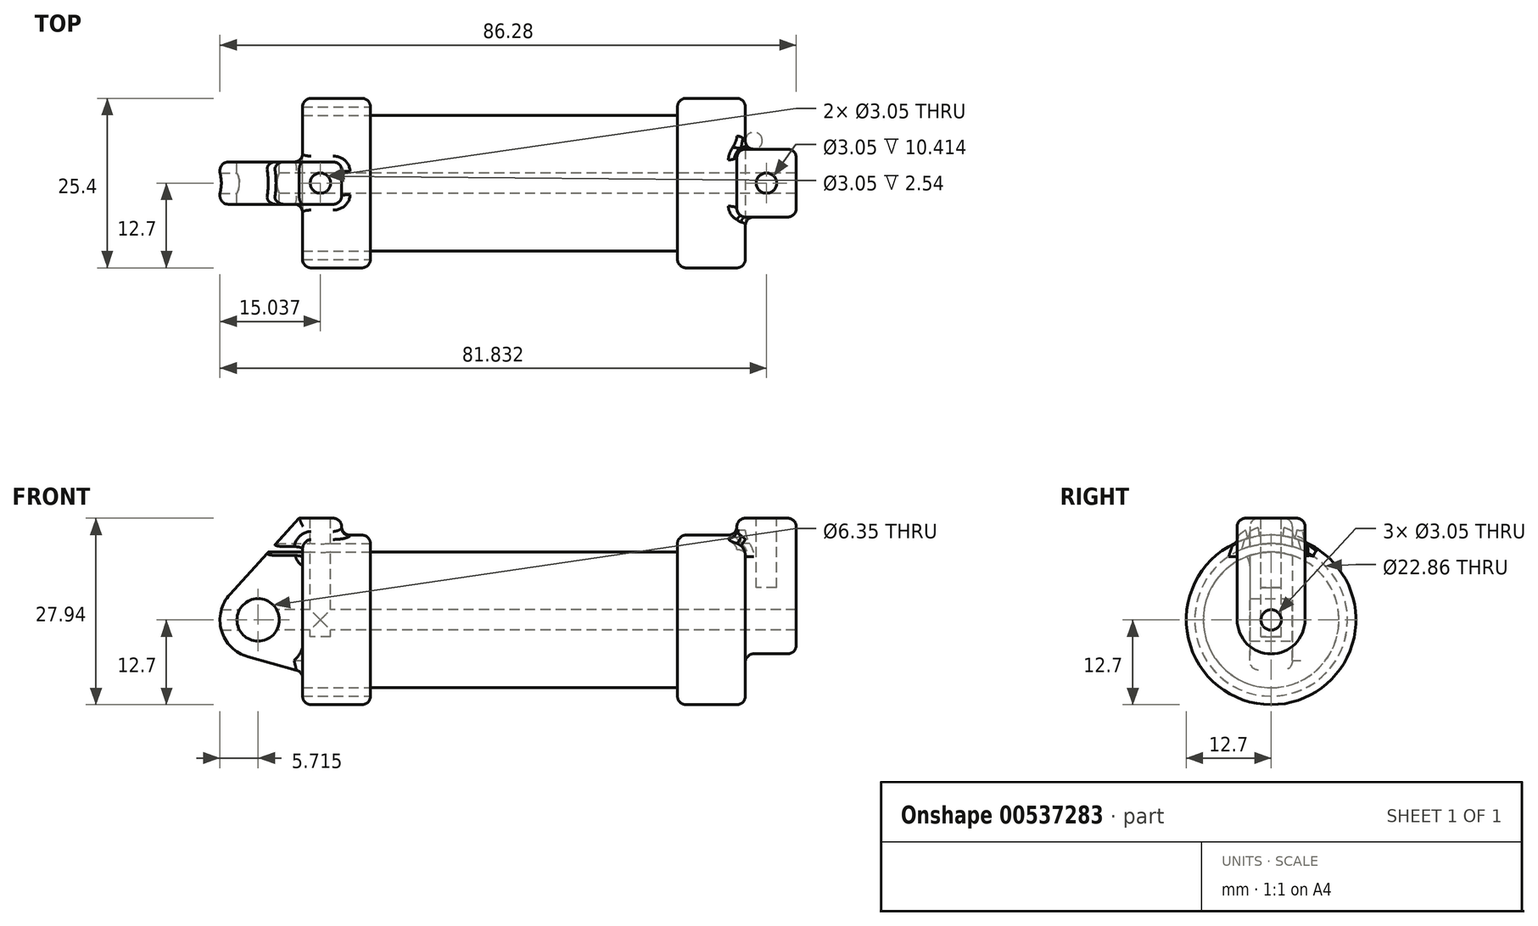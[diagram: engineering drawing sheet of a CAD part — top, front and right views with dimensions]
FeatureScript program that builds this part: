
annotation { "Feature Type Name" : "Feature", "Feature Type Description" : "" }
export const myFeature = defineFeature(function(context is Context, id is Id, definition is map)
    precondition{}
    {
        {
            var Q0;
            Q0=qCreatedBy(makeId("Front.planeOp"),FACE);
            var sketch = newSketch(context, id + "F0", { "sketchPlane" : qUnion([Q0])});
            skLineSegment(sketch, "E0", {"start": v(0, 0) * mm, "end": v(0, 12.7) * mm});
            skLineSegment(sketch, "E1", {"start": v(0, 12.7) * mm, "end": v(10.16, 12.7) * mm});
            skLineSegment(sketch, "E2", {"start": v(10.16, 12.7) * mm, "end": v(10.16, 10.16) * mm});
            skLineSegment(sketch, "E3", {"start": v(10.16, 10.16) * mm, "end": v(56.13, 10.16) * mm});
            skLineSegment(sketch, "E4", {"start": v(56.13, 10.16) * mm, "end": v(56.13, 12.7) * mm});
            skLineSegment(sketch, "E5", {"start": v(56.13, 12.7) * mm, "end": v(66.3, 12.7) * mm});
            skLineSegment(sketch, "E6", {"start": v(66.3, 12.7) * mm, "end": v(66.3, 0) * mm});
            skLineSegment(sketch, "E7", {"start": v(66.3, 0) * mm, "end": v(0, 0) * mm});
            skLineSegment(sketch, "E8", {"start": v(5.84, 15.24) * mm, "end": v(-0.5, 15.24) * mm});
            skLineSegment(sketch, "E9", {"start": v(-0.5, 15.24) * mm, "end": v(-10.88, 3.85) * mm});
            skLineSegment(sketch, "E10", {"start": v(0, 0) * mm, "end": v(-6.65, 0) * mm});
            skCircle(sketch, "E11", {"center": v(-6.65, 0) * mm, "radius": 5.72 * mm});
            skCircle(sketch, "E12", {"center": v(-6.65, 0) * mm, "radius": 3.18 * mm});
            skLineSegment(sketch, "E13", {"start": v(5.84, 15.24) * mm, "end": v(5.84, -9.4) * mm});
            skLineSegment(sketch, "E14", {"start": v(5.84, -9.4) * mm, "end": v(-8.18, -5.5) * mm});
            skSolve(sketch);
        }
        {
            var Q0;
            {var subQ0=sQuery(id+"F0.wireOp",EDGE,"E2");Q0=makeQuery(id+"F0.imprint","IMPRINT",FACE,{"disambiguationData":[TD([[makeQuery(id+"F0.imprint","IMPRINT",EDGE,{"derivedFrom":subQ0}),-1.0]])]});}
            var Q1;
            {var subQ0=sQuery(id+"F0.wireOp",EDGE,"E0");Q1=makeQuery(id+"F0.imprint","IMPRINT",FACE,{"disambiguationData":[TD([[makeQuery(id+"F0.imprint","IMPRINT",EDGE,{"derivedFrom":subQ0}),-1.0]])]});}
            var Q2;
            Q2=sQuery(id+"F0.wireOp",EDGE,"E7");
            revolve(context, id + "F1", {"entities" : qUnion([Q0, Q1]), "axis" : qUnion([Q2]), "revolveType" : RevolveType.FULL});
        }
        {
            var Q0;
            {var subQ1=sQuery(id+"F0.wireOp",EDGE,"E0");Q0=makeQuery(id+"F0.imprint","IMPRINT",FACE,{"disambiguationData":[TD([[makeQuery(id+"F0.imprint","IMPRINT",EDGE,{"derivedFrom":subQ1}),1.0]])]});}
            var Q1;
            {var subQ0=sQuery(id+"F0.wireOp",EDGE,"E14");Q1=makeQuery(id+"F0.imprint","IMPRINT",FACE,{"disambiguationData":[TD([[makeQuery(id+"F0.imprint","IMPRINT",EDGE,{"derivedFrom":subQ0}),-1.0]])]});}
            var Q2;
            {var subQ5=sQuery(id+"F0.wireOp",EDGE,"E12");Q2=makeQuery(id+"F0.imprint","IMPRINT",FACE,{"disambiguationData":[TD([[makeQuery(id+"F0.imprint","IMPRINT",EDGE,{"derivedFrom":subQ5}),-1.0]])]});}
            var Q3;
            {var subQ0=sQuery(id+"F0.wireOp",EDGE,"E0");Q3=makeQuery(id+"F0.imprint","IMPRINT",FACE,{"disambiguationData":[TD([[makeQuery(id+"F0.imprint","IMPRINT",EDGE,{"derivedFrom":subQ0}),-1.0]])]});}
            extrude(context, id + "F2", {"entities" : qUnion([Q0, Q1, Q2, Q3]), "operationType" : NewBodyOperationType.ADD, "endBound" : BoundingType.SYMMETRIC, "depth" : 6.35 * mm, "offsetDistance" : 25.4 * mm});
        }
        {
            var Q0;
            Q0=makeQuery(id+"F1.opRevolve","SWEPT_FACE",FACE,{"disambiguationData":[OSD([sQuery(id+"F0.wireOp",EDGE,"E6")])]});
            var sketch = newSketch(context, id + "F3", { "sketchPlane" : qUnion([Q0])});
            skCircle(sketch, "E15", {"center": v(0, 0) * mm, "radius": 1.52 * mm});
            skCircle(sketch, "E16", {"center": v(0, 0) * mm, "radius": 5.08 * mm});
            skLineSegment(sketch, "E17", {"start": v(-5.08, 0) * mm, "end": v(-5.08, 15.24) * mm});
            skLineSegment(sketch, "E18", {"start": v(5.08, 0) * mm, "end": v(5.08, 15.24) * mm});
            skLineSegment(sketch, "E19", {"start": v(-5.08, 15.24) * mm, "end": v(5.08, 15.24) * mm});
            skSolve(sketch);
        }
        {
            var Q0;
            {var subQ0=sQuery(id+"F3.wireOp",EDGE,"E17");var subQ1=sQuery(id+"F3.wireOp",EDGE,"E16");var subQ2=makeQuery(id+"F3.imprint","INTERSECT",VERTEX,{"derivedFrom":[subQ1,subQ0]});Q0=makeQuery(id+"F3.imprint","IMPRINT",FACE,{"disambiguationData":[TD([[makeQuery(id+"F3.imprint","IMPRINT",EDGE,{"disambiguationData":[TD([[subQ2,1.0]])],"derivedFrom":subQ1}),-1.0]])]});}
            var Q1;
            Q1=makeQuery(id+"F3.imprint","IMPRINT",FACE,{"disambiguationData":[TD([[makeQuery(id+"F3.imprint","IMPRINT",EDGE,{"derivedFrom":sQuery(id+"F3.wireOp",EDGE,"E15")}),-1.0]])]});
            var Q2;
            {var subQ0=sQuery(id+"F3.wireOp",EDGE,"E19");Q2=makeQuery(id+"F3.imprint","IMPRINT",FACE,{"disambiguationData":[TD([[makeQuery(id+"F3.imprint","IMPRINT",EDGE,{"derivedFrom":subQ0}),-1.0]])]});}
            extrude(context, id + "F4", {"entities" : qUnion([Q0, Q1, Q2]), "operationType" : NewBodyOperationType.ADD, "depth" : 7.62 * mm, "offsetDistance" : 25.4 * mm, "hasSecondDirection" : true, "secondDirectionOppositeDirection" : true, "secondDirectionDepth" : 1.27 * mm});
        }
        {
            var Q0;
            Q0=makeQuery(id+"F4.boolean.opBoolean","SPLIT",FACE,{"disambiguationData":[TD([makeQuery(id+"F4.opExtrude","SWEPT_FACE",FACE,{"disambiguationData":[OSD([sQuery(id+"F3.wireOp",EDGE,"E15")])]})])],"derivedFrom":makeQuery(id+"F1.opRevolve","SWEPT_FACE",FACE,{"disambiguationData":[OSD([sQuery(id+"F0.wireOp",EDGE,"E6")])]})});
            extrude(context, id + "F5", {"entities" : qUnion([Q0]), "operationType" : NewBodyOperationType.REMOVE, "endBound" : BoundingType.THROUGH_ALL, "oppositeDirection" : true, "depth" : 25.4 * mm, "offsetDistance" : 25.4 * mm});
        }
        {
            var Q0;
            Q0=makeQuery(id+"F2.opExtrude","SWEPT_FACE",FACE,{"disambiguationData":[OSD([sQuery(id+"F0.wireOp",EDGE,"E8")])]});
            var sketch = newSketch(context, id + "F6", { "sketchPlane" : qUnion([Q0])});
            skCircle(sketch, "E20", {"center": v(2.67, 0) * mm, "radius": 1.52 * mm});
            skPoint(sketch, "E20.centerSnap0", {"position": v(-0.5, 0) * mm});
            skPoint(sketch, "E20.centerSnap1", {"position": v(2.67, -3.18) * mm});
            skPoint(sketch, "E21.endSnap0", {"position": v(5.84, 0) * mm});
            skCircle(sketch, "E22", {"center": v(69.46, 0) * mm, "radius": 1.52 * mm});
            skSolve(sketch);
        }
        {
            var Q0;
            Q0=makeQuery(id+"F6.imprint","IMPRINT",FACE,{"disambiguationData":[TD([[makeQuery(id+"F6.imprint","IMPRINT",EDGE,{"derivedFrom":sQuery(id+"F6.wireOp",EDGE,"E22")}),1.0]])]});
            var Q1;
            Q1=sQuery(id+"F6.wireOp",EDGE,"E22");
            extrude(context, id + "F7", {"entities" : qUnion([Q0]), "operationType" : NewBodyOperationType.REMOVE, "surfaceEntities" : qUnion([Q1]), "oppositeDirection" : true, "depth" : 10.4 * mm, "offsetDistance" : 25.4 * mm});
        }
        {
            var Q0;
            Q0=makeQuery(id+"F2.boolean.opBoolean","INTERSECT",EDGE,{"derivedFrom":[makeQuery(id+"F1.opRevolve","SWEPT_FACE",FACE,{"disambiguationData":[OSD([sQuery(id+"F0.wireOp",EDGE,"E1")])]}),makeQuery(id+"F2.opExtrude","CAP_FACE",FACE,{"disambiguationData":[OSD([sQuery(id+"F0.wireOp",EDGE,"E8"),sQuery(id+"F0.wireOp",EDGE,"E9"),sQuery(id+"F0.wireOp",EDGE,"E11"),sQuery(id+"F0.wireOp",EDGE,"E12"),sQuery(id+"F0.wireOp",EDGE,"E13"),sQuery(id+"F0.wireOp",EDGE,"E14")])],"isStart":false})]});
            var Q1;
            Q1=makeQuery(id+"F2.opExtrude","CAP_EDGE",EDGE,{"disambiguationData":[OSD([sQuery(id+"F0.wireOp",EDGE,"E8")])],"isStart":false});
            var Q2;
            Q2=makeQuery(id+"F2.opExtrude","CAP_EDGE",EDGE,{"disambiguationData":[OSD([sQuery(id+"F0.wireOp",EDGE,"E9")])],"isStart":false});
            var Q3;
            Q3=makeQuery(id+"F2.opExtrude","CAP_EDGE",EDGE,{"disambiguationData":[OSD([sQuery(id+"F0.wireOp",EDGE,"E11")])],"isStart":false});
            var Q4;
            Q4=makeQuery(id+"F2.opExtrude","CAP_EDGE",EDGE,{"disambiguationData":[OSD([sQuery(id+"F0.wireOp",EDGE,"E14")])],"isStart":false});
            var Q5;
            Q5=makeQuery(id+"F2.opExtrude","CAP_EDGE",EDGE,{"disambiguationData":[OSD([sQuery(id+"F0.wireOp",EDGE,"E9")])],"isStart":true});
            var Q6;
            Q6=makeQuery(id+"F2.boolean.opBoolean","INTERSECT",EDGE,{"derivedFrom":[makeQuery(id+"F1.opRevolve","SWEPT_FACE",FACE,{"disambiguationData":[OSD([sQuery(id+"F0.wireOp",EDGE,"E0")])]}),makeQuery(id+"F2.opExtrude","CAP_FACE",FACE,{"disambiguationData":[OSD([sQuery(id+"F0.wireOp",EDGE,"E8"),sQuery(id+"F0.wireOp",EDGE,"E9"),sQuery(id+"F0.wireOp",EDGE,"E11"),sQuery(id+"F0.wireOp",EDGE,"E12"),sQuery(id+"F0.wireOp",EDGE,"E13"),sQuery(id+"F0.wireOp",EDGE,"E14")])],"isStart":true})]});
            var Q7;
            Q7=makeQuery(id+"F2.opExtrude","CAP_EDGE",EDGE,{"disambiguationData":[OSD([sQuery(id+"F0.wireOp",EDGE,"E11")])],"isStart":true});
            var Q8;
            Q8=makeQuery(id+"F2.opExtrude","CAP_EDGE",EDGE,{"disambiguationData":[OSD([sQuery(id+"F0.wireOp",EDGE,"E14")])],"isStart":true});
            var Q9;
            Q9=makeQuery(id+"F2.boolean.opBoolean","INTERSECT",EDGE,{"derivedFrom":[makeQuery(id+"F1.opRevolve","SWEPT_FACE",FACE,{"disambiguationData":[OSD([sQuery(id+"F0.wireOp",EDGE,"E0")])]}),makeQuery(id+"F2.opExtrude","SWEPT_FACE",FACE,{"disambiguationData":[OSD([sQuery(id+"F0.wireOp",EDGE,"E14")])]})]});
            var Q10;
            Q10=makeQuery(id+"F1.opRevolve","SWEPT_EDGE",EDGE,{"disambiguationData":[OSD([sQuery(id+"F0.wireOp",EDGE,"E1"),sQuery(id+"F0.wireOp",EDGE,"E2")])]});
            var Q11;
            Q11=makeQuery(id+"F1.opRevolve","SWEPT_FACE",FACE,{"disambiguationData":[OSD([sQuery(id+"F0.wireOp",EDGE,"E1")])]});
            var Q12;
            Q12=makeQuery(id+"F1.opRevolve","SWEPT_EDGE",EDGE,{"disambiguationData":[OSD([sQuery(id+"F0.wireOp",EDGE,"E0"),sQuery(id+"F0.wireOp",EDGE,"E1")])]});
            var Q13;
            Q13=makeQuery(id+"F1.opRevolve","SWEPT_EDGE",EDGE,{"disambiguationData":[OSD([sQuery(id+"F0.wireOp",EDGE,"E4"),sQuery(id+"F0.wireOp",EDGE,"E5")])]});
            var Q14;
            Q14=makeQuery(id+"F4.opExtrude","CAP_EDGE",EDGE,{"disambiguationData":[OSD([sQuery(id+"F3.wireOp",EDGE,"E17")])],"isStart":true});
            var Q15;
            Q15=makeQuery(id+"F4.opExtrude","SWEPT_EDGE",EDGE,{"disambiguationData":[OSD([sQuery(id+"F3.wireOp",EDGE,"E18"),sQuery(id+"F3.wireOp",EDGE,"E19")])]});
            var Q16;
            Q16=makeQuery(id+"F4.opExtrude","SWEPT_EDGE",EDGE,{"disambiguationData":[OSD([sQuery(id+"F3.wireOp",EDGE,"E17"),sQuery(id+"F3.wireOp",EDGE,"E19")])]});
            var Q17;
            Q17=makeQuery(id+"F2.opExtrude","CAP_EDGE",EDGE,{"disambiguationData":[OSD([sQuery(id+"F0.wireOp",EDGE,"E13")])],"isStart":false});
            var Q18;
            Q18=makeQuery(id+"F4.opExtrude","CAP_EDGE",EDGE,{"disambiguationData":[OSD([sQuery(id+"F3.wireOp",EDGE,"E17")])],"isStart":false});
            var Q19;
            Q19=makeQuery(id+"F4.opExtrude","CAP_EDGE",EDGE,{"disambiguationData":[OSD([sQuery(id+"F3.wireOp",EDGE,"E18")])],"isStart":false});
            var Q20;
            Q20=makeQuery(id+"F4.opExtrude","CAP_EDGE",EDGE,{"disambiguationData":[OSD([sQuery(id+"F3.wireOp",EDGE,"E16")])],"isStart":false});
            var Q21;
            Q21=makeQuery(id+"F4.opExtrude","CAP_EDGE",EDGE,{"disambiguationData":[OSD([sQuery(id+"F3.wireOp",EDGE,"E19")])],"isStart":false});
            var Q22;
            Q22=makeQuery(id+"F2.opExtrude","CAP_EDGE",EDGE,{"disambiguationData":[OSD([sQuery(id+"F0.wireOp",EDGE,"E13")])],"isStart":true});
            var Q23;
            Q23=makeQuery(id+"F2.opExtrude","SWEPT_EDGE",EDGE,{"disambiguationData":[OSD([sQuery(id+"F0.wireOp",EDGE,"E8"),sQuery(id+"F0.wireOp",EDGE,"E13")])]});
            var Q24;
            Q24=makeQuery(id+"F2.opExtrude","CAP_EDGE",EDGE,{"disambiguationData":[OSD([sQuery(id+"F0.wireOp",EDGE,"E8")])],"isStart":true});
            fillet(context, id + "F8", {"entities" : qUnion([Q0, Q1, Q2, Q3, Q4, Q5, Q6, Q7, Q8, Q9, Q10, Q11, Q12, Q13, Q14, Q15, Q16, Q17, Q18, Q19, Q20, Q21, Q22, Q23, Q24]), "radius" : 1.27 * mm, "allowEdgeOverflow" : false});
        }
        {
            var Q0;
            Q0=makeQuery(id+"F4.boolean.opBoolean","SPLIT",FACE,{"disambiguationData":[TD([makeQuery(id+"F1.opRevolve","SWEPT_FACE",FACE,{"disambiguationData":[OSD([sQuery(id+"F0.wireOp",EDGE,"E5")])]})])],"derivedFrom":makeQuery(id+"F1.opRevolve","SWEPT_FACE",FACE,{"disambiguationData":[OSD([sQuery(id+"F0.wireOp",EDGE,"E6")])]})});
            var Q1;
            Q1=makeQuery(id+"F8.opFillet","BLEND_FACE",FACE,{"disambiguationData":[OSD([sQuery(id+"F0.wireOp",EDGE,"E5"),sQuery(id+"F3.wireOp",EDGE,"E17")])]});
            var Q2;
            Q2=makeQuery(id+"F4.opExtrude","SWEPT_FACE",FACE,{"disambiguationData":[OSD([sQuery(id+"F3.wireOp",EDGE,"E18")])]});
            fillet(context, id + "F9", {"entities" : qUnion([Q0, Q1, Q2]), "radius" : 1.27 * mm, "tangentPropagation" : true, "allowEdgeOverflow" : false});
        }
        {
            var Q0;
            Q0=makeQuery(id+"F6.imprint","IMPRINT",FACE,{"disambiguationData":[TD([[makeQuery(id+"F6.imprint","IMPRINT",EDGE,{"derivedFrom":sQuery(id+"F6.wireOp",EDGE,"E20")}),1.0]])]});
            extrude(context, id + "F10", {"entities" : qUnion([Q0]), "operationType" : NewBodyOperationType.REMOVE, "oppositeDirection" : true, "depth" : 17.78 * mm, "offsetDistance" : 25.4 * mm});
        }
        {
            var Q0;
            Q0=makeQuery(id+"F1.opRevolve","SWEPT_FACE",FACE,{"disambiguationData":[OSD([sQuery(id+"F0.wireOp",EDGE,"E2")])]});
            extrude(context, id + "F11", {"entities" : qUnion([Q0]), "operationType" : NewBodyOperationType.REMOVE, "oppositeDirection" : true, "depth" : 25.4 * mm, "offsetDistance" : 25.4 * mm});
        }
    });
